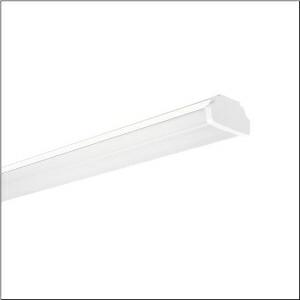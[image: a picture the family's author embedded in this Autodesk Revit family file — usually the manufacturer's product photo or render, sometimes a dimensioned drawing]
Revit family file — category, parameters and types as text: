
# Revit family: modario_r__31_ho_53bm813d2v4120_b0b8
name_source: partatom
category: Lighting Fixtures
units: mm (PartAtom-declared; Revit-internal decimal feet)

## family parameters
Cut with Voids When Loaded = No
Host = Face
Light Source = No
Part Type = Normal
Room Calculation Point = No
Round Connector Dimension = Use Diameter
Shared = No

## types (1)
- --- (1 x LED, 12260 lm, 79.4 W, 4000K)
    Apparent Load = 79 VA
    CIE Flux Codes = 62 84 96 93 100
    Color Rendering = 80
    Color Temperature = 4000K
    Default Elevation = 1800 mm
    Description = Modario® 31 HOluminaire insert, length: 1.495mm, width: 81mm, height: 82mm, LED rated luminous flux: 12.260lm, light colour: 840, control gear: DALI 2, control gear: ECG DALI, with plug, 5-pole, with phase selection, mains connection: 220..240V, AC, 50/60Hz, primary optical cover: cover, of PMMA, light emission: direct distribution, primary light characteristic: symmetric, protection rating (complete): IP20, protection rating (LED compartment): IP50, insulation class (complete): insulation class I (protective earthing), certification: CE, ENEC, VDE, permissible ambient temperature for indoor applications: -25..+30°C, corresponds to IFS (International Featured Standards) requirements for safety and quality in the food industry, reducing of maximum allowable ambient temperature of 5°C with ceiling mounting, packaging unit: 1 piece
    Height = 92 mm
    Lamp = 1 x LED
    Lamp Light Flux = 12260 lm
    Lamp Power = 79.4 W
    Lamp count = 1
    Length = 1495 mm
    Luminous efficacy = 154 lm/W
    Manufacturer = Siteco
    ModVariant = No
    Model = 53BM813D2V4120
    Mounting Place = Ceiling
    Mounting Type = Pendant
    Number of Poles = 1
    OnlyDefault = Yes
    Power Factor = 1
    Product Name = Modario® 31 HO
    Product group = luminaire insert
    ProductGroupID = 902
    Protection Class = Protection class I
    Protection Degree = IP 20
    RLX_Detail_Level = 1
    RlxData = <blob elided: 42317 chars, md5=6fd46aec>
    Socket = socket
    Standby Power = 0 W
    System Light Flux = 12260 lm
    System Power = 79 W
    Type Comments = factory setting: luminous flux: 100 % | dim-lin: 254 | 345 mA
    Type Image = l_1003447.jpg
    URL = http://relux.com
    VarID = @adj_133661
    Voltage = 0 V
    Weight = 0.00 kg
    Width = 81 mm

## geometry (parser evidence)
native form markers: Blend x4, Sweep x12
no freeform markers — native parametric forms only
